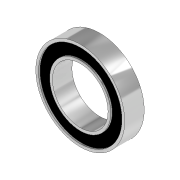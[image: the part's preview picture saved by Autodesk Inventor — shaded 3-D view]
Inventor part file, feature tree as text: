
AUTODESK INVENTOR PART (.ipt)
format: ipt  version: 2020 (Build 240168000, 168)  size: 125,440 bytes
history: native  units: in
note: dims shown in document units (in); Inventor stores cm internally (conversion verified against a paired STEP export)
features: extrude x3, sketch x3, projected_geometry x2
ambient origin geometry x8: Origin, YZ Plane, XZ Plane, XY Plane, X Axis, Y Axis, Z Axis, Center Point
bodies: Solid1 (feature_tree)
feature tree (8):
  extrude  "Extrusion1"  Depth=1.2598in
  extrude  "Extrusion2"  Depth=0.2756in
  extrude  "Extrusion3"  Depth=0.0197in TaperAngle=0.0deg
  sketch  "Sketch1"  dims[d0=0.7874in d1=1.2598in]
  sketch  "Sketch2"  dims[d2=0.2756in d3=0.0in d4=0.0394in]
  projected_geometry  "Projected Loop1"
  sketch  "Sketch3"  dims[d5=0.0394in d6=0.0197in d7=0.0in d8=0.0197in d9=0.0in]
  projected_geometry  "Projected Loop2"
